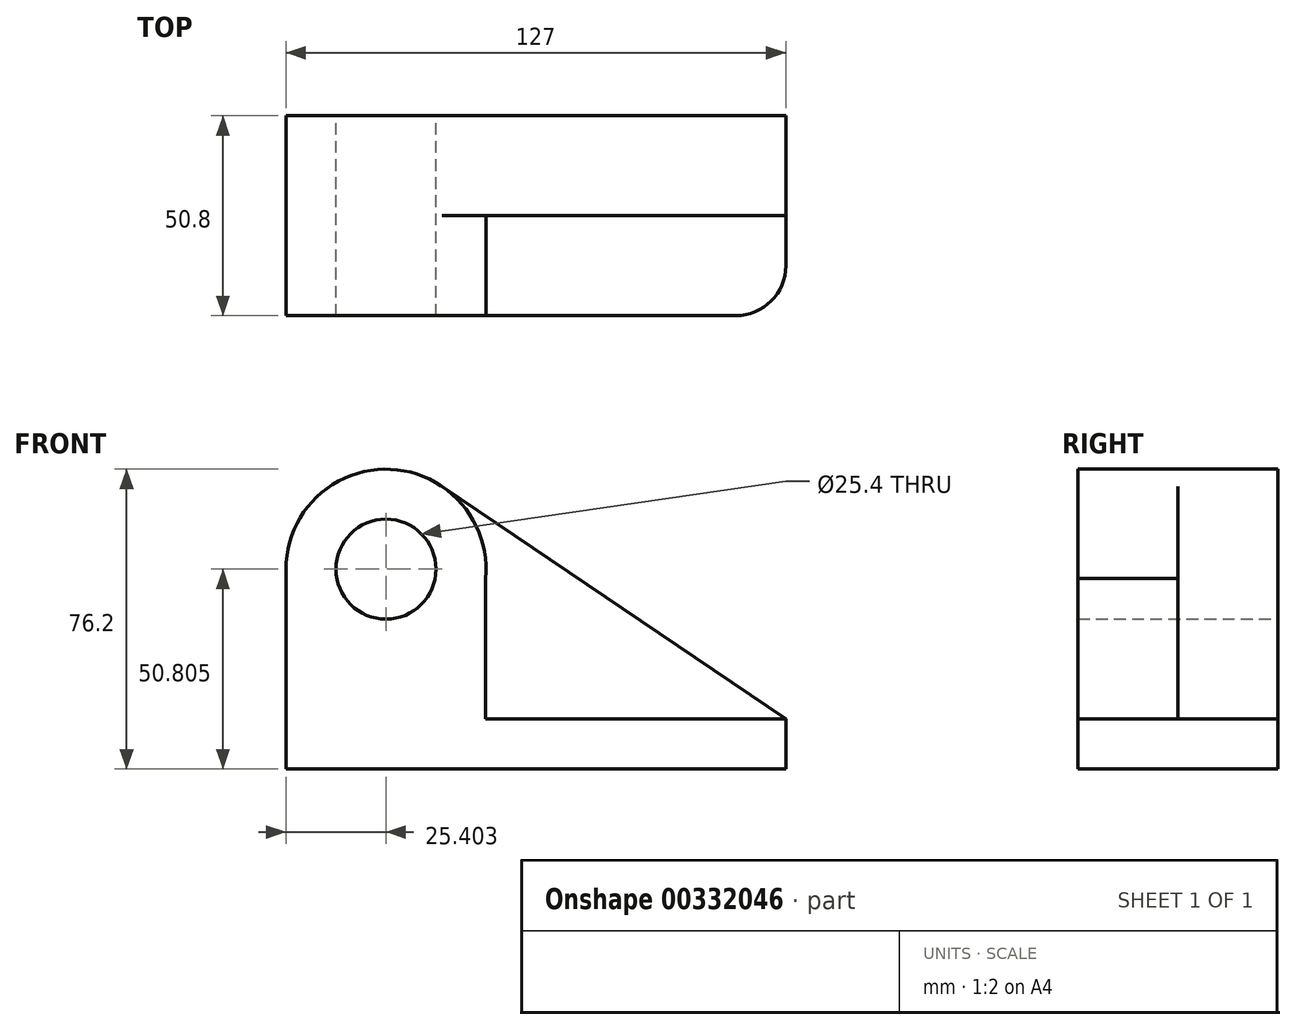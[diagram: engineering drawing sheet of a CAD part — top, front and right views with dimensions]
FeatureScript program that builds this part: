
annotation { "Feature Type Name" : "Feature", "Feature Type Description" : "" }
export const myFeature = defineFeature(function(context is Context, id is Id, definition is map)
    precondition{}
    {
        {
            var Q0;
            Q0=qCreatedBy(makeId("Front.planeOp"),FACE);
            var sketch = newSketch(context, id + "F0", { "sketchPlane" : qUnion([Q0])});
            skCircle(sketch, "E0", {"center": v(-43.44, 2.4) * mm, "radius": 12.7 * mm});
            skArc(sketch, "E1", {"start": v(-29.2, 23.44) * mm, "mid": v(-55.34, 24.84) * mm, "end": v(-68.84, 2.4) * mm});
            skLineSegment(sketch, "E2", {"start": v(-68.84, 2.4) * mm, "end": v(-68.84, -48.4) * mm});
            skLineSegment(sketch, "E3", {"start": v(-68.84, -48.4) * mm, "end": v(58.16, -48.4) * mm});
            skLineSegment(sketch, "E4", {"start": v(58.16, -48.4) * mm, "end": v(58.16, -35.7) * mm});
            skLineSegment(sketch, "E5", {"start": v(58.16, -35.7) * mm, "end": v(-29.2, 23.44) * mm});
            skSolve(sketch);
        }
        {
            var Q0;
            Q0=makeQuery(id+"F0.imprint","IMPRINT",FACE,{"disambiguationData":[TD([[makeQuery(id+"F0.imprint","IMPRINT",EDGE,{"derivedFrom":sQuery(id+"F0.wireOp",EDGE,"E0")}),-1.0]])]});
            extrude(context, id + "F1", {"entities" : qUnion([Q0]), "depth" : 25.4 * mm});
        }
        {
            var Q0;
            Q0=makeQuery(id+"F1.opExtrude","CAP_FACE",FACE,{"disambiguationData":[OSD([sQuery(id+"F0.wireOp",EDGE,"E0"),sQuery(id+"F0.wireOp",EDGE,"E1"),sQuery(id+"F0.wireOp",EDGE,"E2"),sQuery(id+"F0.wireOp",EDGE,"E3"),sQuery(id+"F0.wireOp",EDGE,"E4"),sQuery(id+"F0.wireOp",EDGE,"E5")])],"isStart":false});
            var sketch = newSketch(context, id + "F2", { "sketchPlane" : qUnion([Q0])});
            skCircle(sketch, "E6", {"center": v(-43.44, 2.4) * mm, "radius": 12.7 * mm});
            skArc(sketch, "E7", {"start": v(-18.15, 0) * mm, "mid": v(-42.23, 27.78) * mm, "end": v(-68.84, 2.4) * mm});
            skLineSegment(sketch, "E8.bottom", {"start": v(58.16, -35.7) * mm, "end": v(-18.15, -35.7) * mm});
            skLineSegment(sketch, "E8.top", {"start": v(58.16, -35.7) * mm, "end": v(-18.15, -35.7) * mm});
            skLineSegment(sketch, "E8.left", {"start": v(58.16, -35.7) * mm, "end": v(58.16, -35.7) * mm});
            skLineSegment(sketch, "E8.right", {"start": v(-68.84, -35.7) * mm, "end": v(-68.84, -35.7) * mm});
            skLineSegment(sketch, "E9", {"start": v(-30.97, 0) * mm, "end": v(-26.31, 11.74) * mm});
            skLineSegment(sketch, "E10", {"start": v(-18.15, 0) * mm, "end": v(-18.15, -35.7) * mm});
            skLineSegment(sketch, "E11", {"start": v(-68.84, 2.4) * mm, "end": v(-68.84, -35.7) * mm});
            skSolve(sketch);
        }
        {
            var Q0;
            Q0=makeQuery(id+"F2.imprint","IMPRINT",FACE,{"disambiguationData":[TD([[makeQuery(id+"F2.imprint","IMPRINT",EDGE,{"derivedFrom":sQuery(id+"F2.wireOp",EDGE,"E6")}),-1.0]])]});
            extrude(context, id + "F3", {"entities" : qUnion([Q0]), "operationType" : NewBodyOperationType.ADD, "depth" : 25.4 * mm});
        }
        {
            var Q0;
            Q0=makeQuery(id+"F3.opExtrude","CAP_EDGE",EDGE,{"disambiguationData":[OSD([sQuery(id+"F0.wireOp",EDGE,"E4")])],"isStart":false});
            fillet(context, id + "F4", {"entities" : qUnion([Q0]), "radius" : 12.7 * mm, "tangentPropagation" : true, "allowEdgeOverflow" : false});
        }
    });
